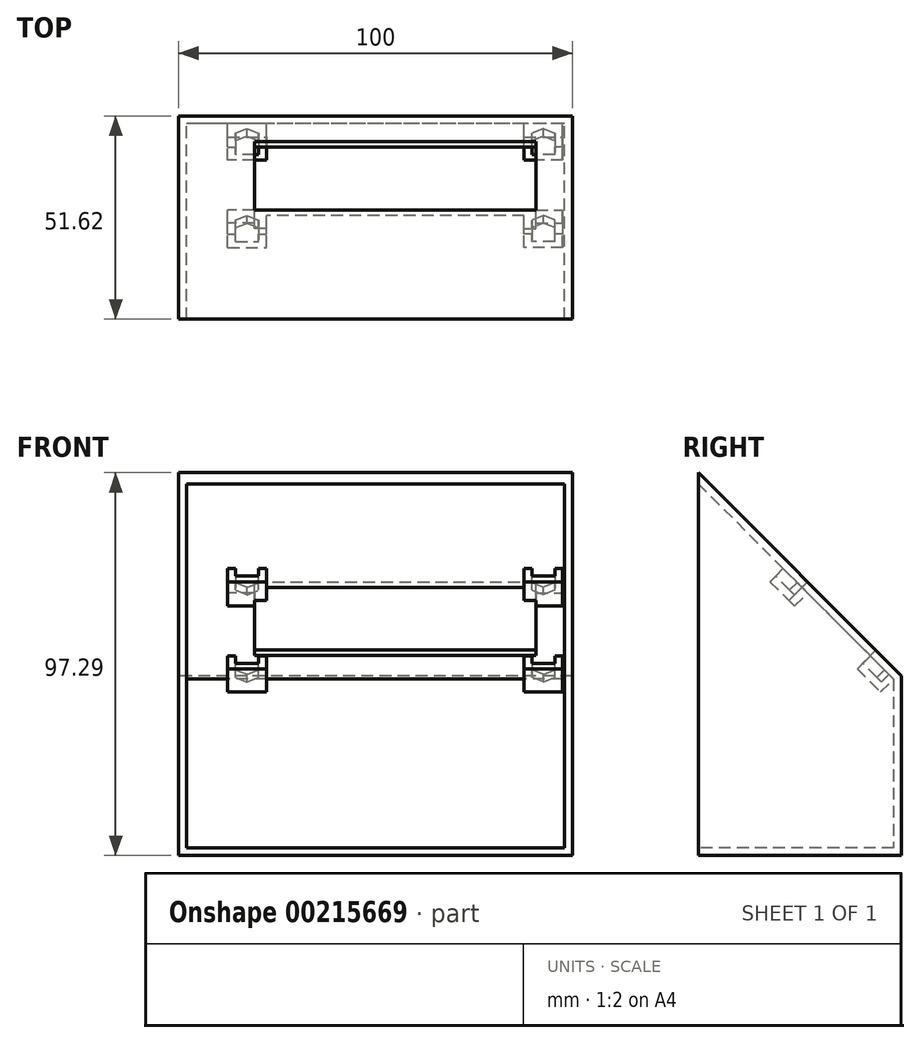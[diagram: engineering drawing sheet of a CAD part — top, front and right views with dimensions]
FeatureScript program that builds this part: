
annotation { "Feature Type Name" : "Feature", "Feature Type Description" : "" }
export const myFeature = defineFeature(function(context is Context, id is Id, definition is map)
    precondition{}
    {
        {
            var Q0;
            Q0=qCreatedBy(makeId("Top.planeOp"),FACE);
            var sketch = newSketch(context, id + "F0", { "sketchPlane" : qUnion([Q0])});
            skLineSegment(sketch, "E0.bottom", {"start": v(-35.75, 63.75) * mm, "end": v(35.75, 63.75) * mm});
            skLineSegment(sketch, "E0.top", {"start": v(-35.75, 39.25) * mm, "end": v(35.75, 39.25) * mm});
            skLineSegment(sketch, "E0.left", {"start": v(-35.75, 63.75) * mm, "end": v(-35.75, 39.25) * mm});
            skLineSegment(sketch, "E0.right", {"start": v(35.75, 63.75) * mm, "end": v(35.75, 39.25) * mm});
            skPoint(sketch, "E0.middle", {"position": v(0, 51.5) * mm});
            skLineSegment(sketch, "E1.bottom", {"start": v(-45, 73) * mm, "end": v(45, 73) * mm});
            skLineSegment(sketch, "E1.left", {"start": v(-45, 73) * mm, "end": v(-45, 30) * mm});
            skLineSegment(sketch, "E1.right", {"start": v(45, 73) * mm, "end": v(45, 30) * mm});
            skLineSegment(sketch, "E2.top", {"start": v(-45, 0) * mm, "end": v(45, 0) * mm});
            skLineSegment(sketch, "E2.left", {"start": v(-45, 30) * mm, "end": v(-45, 0) * mm});
            skLineSegment(sketch, "E2.right", {"start": v(45, 30) * mm, "end": v(45, 0) * mm});
            skSolve(sketch);
        }
        {
            var Q0;
            Q0=qCreatedBy(makeId("Right.planeOp"),FACE);
            var sketch = newSketch(context, id + "F1", { "sketchPlane" : qUnion([Q0])});
            skLineSegment(sketch, "E3", {"start": v(0, 0) * mm, "end": v(51.62, -51.62) * mm});
            skLineSegment(sketch, "E4", {"start": v(51.62, -51.62) * mm, "end": v(51.62, -97.29) * mm});
            skLineSegment(sketch, "E5", {"start": v(51.62, -97.29) * mm, "end": v(0, -97.29) * mm});
            skLineSegment(sketch, "E6", {"start": v(0, -97.29) * mm, "end": v(0, 0) * mm});
            skSolve(sketch);
        }
        {
            var Q0;
            Q0=makeQuery(id+"F1.imprint","IMPRINT",FACE,{"disambiguationData":[TD([[makeQuery(id+"F1.imprint","IMPRINT",EDGE,{"derivedFrom":sQuery(id+"F1.wireOp",EDGE,"E3")}),-1.0]])]});
            extrude(context, id + "F2", {"entities" : qUnion([Q0]), "endBound" : BoundingType.SYMMETRIC, "depth" : 90 * mm});
        }
        {
            var Q0;
            Q0=makeQuery(id+"F2.opExtrude","CAP_FACE",FACE,{"disambiguationData":[OSD([sQuery(id+"F1.wireOp",EDGE,"E3"),sQuery(id+"F1.wireOp",EDGE,"E4"),sQuery(id+"F1.wireOp",EDGE,"E5"),sQuery(id+"F1.wireOp",EDGE,"E6")])],"isStart":true});
            var sketch = newSketch(context, id + "F3", { "sketchPlane" : qUnion([Q0])});
            skLineSegment(sketch, "E7", {"start": v(-51.62, -97.29) * mm, "end": v(0, -97.29) * mm});
            skLineSegment(sketch, "E8", {"start": v(0, -97.29) * mm, "end": v(0, 0) * mm});
            skLineSegment(sketch, "E9", {"start": v(0, 0) * mm, "end": v(-51.62, -51.62) * mm});
            skLineSegment(sketch, "E10", {"start": v(-51.62, -51.62) * mm, "end": v(-51.62, -97.29) * mm});
            skSolve(sketch);
        }
        {
            var Q0;
            Q0 = qSketchRegion(id + "F3", true);
            extrude(context, id + "F4", {"entities" : qUnion([Q0]), "operationType" : NewBodyOperationType.ADD, "depth" : 10 * mm});
        }
        {
            var Q0;
            Q0=makeQuery(id+"F2.opExtrude","SWEPT_FACE",FACE,{"disambiguationData":[OSD([sQuery(id+"F1.wireOp",EDGE,"E3")])]});
            var sketch = newSketch(context, id + "F5", { "sketchPlane" : qUnion([Q0])});
            skLineSegment(sketch, "E11.bottom", {"start": v(35.75, -63.75) * mm, "end": v(-35.75, -63.75) * mm});
            skLineSegment(sketch, "E11.top", {"start": v(35.75, -39.25) * mm, "end": v(-35.75, -39.25) * mm});
            skLineSegment(sketch, "E11.left", {"start": v(35.75, -63.75) * mm, "end": v(35.75, -39.25) * mm});
            skLineSegment(sketch, "E11.right", {"start": v(-35.75, -63.75) * mm, "end": v(-35.75, -39.25) * mm});
            skPoint(sketch, "E11.middle", {"position": v(0, -51.5) * mm});
            skSolve(sketch);
        }
        {
            var Q0;
            Q0=makeQuery(id+"F2.opExtrude","SWEPT_FACE",FACE,{"disambiguationData":[OSD([sQuery(id+"F1.wireOp",EDGE,"E6")])]});
            shell(context, id + "F6", {"entities" : qUnion([Q0]), "thickness" : 2 * mm});
        }
        {
            var Q0;
            Q0=makeQuery(id+"F5.imprint","IMPRINT",FACE,{"disambiguationData":[TD([[makeQuery(id+"F5.imprint","IMPRINT",EDGE,{"derivedFrom":sQuery(id+"F5.wireOp",EDGE,"E11.bottom")}),-1.0]])]});
            extrude(context, id + "F7", {"entities" : qUnion([Q0]), "operationType" : NewBodyOperationType.REMOVE, "endBound" : BoundingType.UP_TO_NEXT, "oppositeDirection" : true, "depth" : 25 * mm});
        }
        {
            var Q0;
            Q0=makeQuery(id+"F6.opShell","OFFSET_FACE",FACE,{"disambiguationData":[OSD([sQuery(id+"F1.wireOp",EDGE,"E3")])]});
            var sketch = newSketch(context, id + "F8", { "sketchPlane" : qUnion([Q0])});
            skCircle(sketch, "E12.cCircle", {"center": v(-37.65, -35.85) * mm, "radius": 2.9 * mm, "construction": true});
            skLineSegment(sketch, "E12.0", {"start": v(-40.55, -37.52) * mm, "end": v(-40.55, -34.18) * mm, "construction": true});
            skLineSegment(sketch, "E12.1", {"start": v(-40.55, -34.18) * mm, "end": v(-37.65, -32.5) * mm, "construction": true});
            skLineSegment(sketch, "E12.2", {"start": v(-37.65, -32.5) * mm, "end": v(-34.75, -34.18) * mm, "construction": true});
            skLineSegment(sketch, "E12.3", {"start": v(-34.75, -34.18) * mm, "end": v(-34.75, -37.52) * mm, "construction": true});
            skLineSegment(sketch, "E12.4", {"start": v(-34.75, -37.52) * mm, "end": v(-37.65, -39.2) * mm, "construction": true});
            skLineSegment(sketch, "E12.5", {"start": v(-37.65, -39.2) * mm, "end": v(-40.55, -37.52) * mm, "construction": true});
            skPoint(sketch, "E12.0.midPoint", {"position": v(-40.55, -35.85) * mm});
            skCircle(sketch, "E13", {"center": v(-37.65, -35.85) * mm, "radius": 1.65 * mm, "construction": true});
            skCircle(sketch, "E14", {"center": v(37.65, -35.85) * mm, "radius": 1.65 * mm, "construction": true});
            skCircle(sketch, "E15", {"center": v(37.65, -67.15) * mm, "radius": 1.65 * mm, "construction": true});
            skCircle(sketch, "E16", {"center": v(-37.65, -67.15) * mm, "radius": 1.65 * mm, "construction": true});
            skLineSegment(sketch, "E17", {"start": v(0, -28.94) * mm, "end": v(0, -58.03) * mm});
            skLineSegment(sketch, "E18", {"start": v(0, -27.94) * mm, "end": v(0, -57.03) * mm});
            skPoint(sketch, "E19", {"position": v(-35.75, -51.5) * mm});
            skPoint(sketch, "E20", {"position": v(-37.65, -37.5) * mm});
            skLineSegment(sketch, "E21.bottom", {"start": v(-42.55, -32.5) * mm, "end": v(-40.55, -32.5) * mm});
            skLineSegment(sketch, "E21.top", {"start": v(-35.75, -39.25) * mm, "end": v(-32.75, -39.25) * mm});
            skLineSegment(sketch, "E21.left", {"start": v(-42.55, -32.5) * mm, "end": v(-42.55, -39.25) * mm});
            skLineSegment(sketch, "E21.right", {"start": v(-32.75, -32.5) * mm, "end": v(-32.75, -39.25) * mm});
            skLineSegment(sketch, "E22", {"start": v(-35.75, -39.25) * mm, "end": v(-35.75, -41.25) * mm});
            skLineSegment(sketch, "E23", {"start": v(-35.75, -41.25) * mm, "end": v(-42.55, -41.25) * mm});
            skLineSegment(sketch, "E24", {"start": v(-42.55, -41.25) * mm, "end": v(-42.55, -39.25) * mm});
            skLineSegment(sketch, "E25", {"start": v(-40.55, -32.5) * mm, "end": v(-40.55, -37.52) * mm});
            skLineSegment(sketch, "E26", {"start": v(-37.65, -39.2) * mm, "end": v(-34.75, -37.52) * mm});
            skLineSegment(sketch, "E27", {"start": v(-40.55, -37.52) * mm, "end": v(-37.65, -39.2) * mm});
            skLineSegment(sketch, "E28", {"start": v(-34.75, -37.52) * mm, "end": v(-34.75, -32.5) * mm});
            skLineSegment(sketch, "E29.trimOffspring", {"start": v(-34.75, -32.5) * mm, "end": v(-32.75, -32.5) * mm});
            skLineSegment(sketch, "E30.MirrorCS", {"start": v(40.55, -32.5) * mm, "end": v(40.55, -37.52) * mm});
            skLineSegment(sketch, "E31.MirrorCS", {"start": v(37.65, -39.2) * mm, "end": v(34.75, -37.52) * mm});
            skLineSegment(sketch, "E32.MirrorCS", {"start": v(40.55, -37.52) * mm, "end": v(37.65, -39.2) * mm});
            skLineSegment(sketch, "E33.MirrorCS", {"start": v(34.75, -37.52) * mm, "end": v(34.75, -32.5) * mm});
            skLineSegment(sketch, "E34.MirrorCS", {"start": v(40.55, -37.52) * mm, "end": v(40.55, -34.18) * mm, "construction": true});
            skLineSegment(sketch, "E35.MirrorCS", {"start": v(42.55, -41.25) * mm, "end": v(42.55, -39.25) * mm});
            skPoint(sketch, "E36.MirrorP", {"position": v(37.65, -37.5) * mm});
            skLineSegment(sketch, "E37.MirrorCS", {"start": v(32.75, -32.5) * mm, "end": v(32.75, -39.25) * mm});
            skPoint(sketch, "E38.MirrorP", {"position": v(40.55, -35.85) * mm});
            skLineSegment(sketch, "E39.MirrorCS", {"start": v(35.75, -41.25) * mm, "end": v(42.55, -41.25) * mm});
            skLineSegment(sketch, "E40.MirrorCS", {"start": v(37.65, -32.5) * mm, "end": v(34.75, -34.18) * mm, "construction": true});
            skLineSegment(sketch, "E41.MirrorCS", {"start": v(40.55, -34.18) * mm, "end": v(37.65, -32.5) * mm, "construction": true});
            skLineSegment(sketch, "E42.MirrorCS", {"start": v(42.55, -32.5) * mm, "end": v(42.55, -39.25) * mm});
            skLineSegment(sketch, "E43.MirrorCS", {"start": v(35.75, -39.25) * mm, "end": v(35.75, -41.25) * mm});
            skCircle(sketch, "E44.MirrorC", {"center": v(37.65, -35.85) * mm, "radius": 2.9 * mm, "construction": true});
            skLineSegment(sketch, "E45.MirrorCS", {"start": v(35.75, -39.25) * mm, "end": v(32.75, -39.25) * mm});
            skLineSegment(sketch, "E46.MirrorCS", {"start": v(34.75, -32.5) * mm, "end": v(32.75, -32.5) * mm});
            skLineSegment(sketch, "E47.MirrorCS", {"start": v(34.75, -37.52) * mm, "end": v(37.65, -39.2) * mm, "construction": true});
            skLineSegment(sketch, "E48.MirrorCS", {"start": v(37.65, -39.2) * mm, "end": v(40.55, -37.52) * mm, "construction": true});
            skLineSegment(sketch, "E49.MirrorCS", {"start": v(34.75, -34.18) * mm, "end": v(34.75, -37.52) * mm, "construction": true});
            skLineSegment(sketch, "E50.MirrorCS", {"start": v(42.55, -32.5) * mm, "end": v(40.55, -32.5) * mm});
            skLineSegment(sketch, "E51", {"start": v(-35.75, -51.5) * mm, "end": v(56.66, -51.5) * mm, "construction": true});
            skLineSegment(sketch, "E52.MirrorCS", {"start": v(-40.55, -68.82) * mm, "end": v(-40.55, -65.48) * mm});
            skLineSegment(sketch, "E53.MirrorCS", {"start": v(-37.65, -63.8) * mm, "end": v(-40.55, -65.48) * mm, "construction": true});
            skLineSegment(sketch, "E54.MirrorCS", {"start": v(-34.75, -65.48) * mm, "end": v(-37.65, -63.8) * mm, "construction": true});
            skLineSegment(sketch, "E55.MirrorCS", {"start": v(-34.75, -65.48) * mm, "end": v(-34.75, -68.82) * mm});
            skLineSegment(sketch, "E56.MirrorCS", {"start": v(-40.55, -68.82) * mm, "end": v(-37.65, -70.5) * mm, "construction": true});
            skLineSegment(sketch, "E57.MirrorCS", {"start": v(-37.65, -70.5) * mm, "end": v(-34.75, -68.82) * mm, "construction": true});
            skPoint(sketch, "E58.orphan", {"position": v(-40.55, -70.5) * mm});
            skPoint(sketch, "E59.orphan", {"position": v(-34.75, -70.5) * mm});
            skLineSegment(sketch, "E60", {"start": v(-40.55, -68.82) * mm, "end": v(-37.65, -70.5) * mm});
            skLineSegment(sketch, "E61", {"start": v(-37.65, -70.5) * mm, "end": v(-34.75, -68.82) * mm});
            skLineSegment(sketch, "E62.bottom", {"start": v(-42.55, -63.8) * mm, "end": v(-40.55, -63.8) * mm});
            skLineSegment(sketch, "E62.top", {"start": v(-42.55, -72.5) * mm, "end": v(-32.75, -72.5) * mm});
            skLineSegment(sketch, "E62.left", {"start": v(-42.55, -63.8) * mm, "end": v(-42.55, -72.5) * mm});
            skLineSegment(sketch, "E62.right", {"start": v(-32.75, -63.8) * mm, "end": v(-32.75, -72.5) * mm});
            skLineSegment(sketch, "E63", {"start": v(-40.55, -65.48) * mm, "end": v(-40.55, -63.8) * mm});
            skLineSegment(sketch, "E64", {"start": v(-34.75, -65.48) * mm, "end": v(-34.75, -63.75) * mm});
            skLineSegment(sketch, "E65.trimOffspring", {"start": v(-34.75, -63.8) * mm, "end": v(-32.75, -63.8) * mm});
            skLineSegment(sketch, "E66.MirrorCS", {"start": v(34.75, -65.48) * mm, "end": v(34.75, -63.75) * mm});
            skLineSegment(sketch, "E67.MirrorCS", {"start": v(34.75, -65.48) * mm, "end": v(34.75, -68.82) * mm});
            skLineSegment(sketch, "E68.MirrorCS", {"start": v(32.75, -63.8) * mm, "end": v(32.75, -72.5) * mm});
            skLineSegment(sketch, "E69.MirrorCS", {"start": v(34.75, -63.8) * mm, "end": v(32.75, -63.8) * mm});
            skLineSegment(sketch, "E70.MirrorCS", {"start": v(42.55, -72.5) * mm, "end": v(32.75, -72.5) * mm});
            skLineSegment(sketch, "E71.MirrorCS", {"start": v(42.55, -63.8) * mm, "end": v(42.55, -72.5) * mm});
            skLineSegment(sketch, "E72.MirrorCS", {"start": v(42.55, -63.8) * mm, "end": v(40.55, -63.8) * mm});
            skLineSegment(sketch, "E73.MirrorCS", {"start": v(40.55, -65.48) * mm, "end": v(40.55, -63.8) * mm});
            skLineSegment(sketch, "E74.MirrorCS", {"start": v(40.55, -68.82) * mm, "end": v(40.55, -65.48) * mm});
            skLineSegment(sketch, "E75.MirrorCS", {"start": v(40.55, -68.82) * mm, "end": v(37.65, -70.5) * mm, "construction": true});
            skLineSegment(sketch, "E76", {"start": v(37.65, -70.5) * mm, "end": v(34.75, -68.82) * mm});
            skLineSegment(sketch, "E77", {"start": v(37.65, -70.5) * mm, "end": v(40.55, -68.82) * mm});
            skSolve(sketch);
        }
        {
            var Q0;
            Q0=makeQuery(id+"F8.imprint","IMPRINT",FACE,{"disambiguationData":[TD([[makeQuery(id+"F8.imprint","IMPRINT",EDGE,{"derivedFrom":sQuery(id+"F8.wireOp",EDGE,"E52.MirrorCS")}),1.0]])]});
            var Q1;
            Q1=makeQuery(id+"F8.imprint","IMPRINT",FACE,{"disambiguationData":[TD([[makeQuery(id+"F8.imprint","IMPRINT",EDGE,{"derivedFrom":sQuery(id+"F8.wireOp",EDGE,"E21.bottom")}),-1.0]])]});
            var Q2;
            Q2=makeQuery(id+"F8.imprint","IMPRINT",FACE,{"disambiguationData":[TD([[makeQuery(id+"F8.imprint","IMPRINT",EDGE,{"derivedFrom":sQuery(id+"F8.wireOp",EDGE,"E30.MirrorCS")}),1.0]])]});
            var Q3;
            {var subQ4=sQuery(id+"F8.wireOp",EDGE,"E67.MirrorCS");Q3=makeQuery(id+"F8.imprint","IMPRINT",FACE,{"disambiguationData":[TD([[makeQuery(id+"F8.imprint","IMPRINT",EDGE,{"derivedFrom":subQ4}),-1.0]])]});}
            extrude(context, id + "F9", {"entities" : qUnion([Q0, Q1, Q2, Q3]), "operationType" : NewBodyOperationType.ADD, "depth" : 2.7 * mm});
        }
        {
            var Q0;
            Q0=makeQuery(id+"F9.opExtrude","CAP_FACE",FACE,{"disambiguationData":[OSD([sQuery(id+"F8.wireOp",EDGE,"E21.bottom"),sQuery(id+"F8.wireOp",EDGE,"E21.top"),sQuery(id+"F8.wireOp",EDGE,"E21.left"),sQuery(id+"F8.wireOp",EDGE,"E21.right"),sQuery(id+"F8.wireOp",EDGE,"E22"),sQuery(id+"F8.wireOp",EDGE,"E23"),sQuery(id+"F8.wireOp",EDGE,"E24"),sQuery(id+"F8.wireOp",EDGE,"E25"),sQuery(id+"F8.wireOp",EDGE,"E26"),sQuery(id+"F8.wireOp",EDGE,"E27"),sQuery(id+"F8.wireOp",EDGE,"E28"),sQuery(id+"F8.wireOp",EDGE,"E29.trimOffspring")])],"isStart":false});
            var sketch = newSketch(context, id + "F10", { "sketchPlane" : qUnion([Q0])});
            skLineSegment(sketch, "E78.bottom", {"start": v(-42.55, -41.25) * mm, "end": v(-35.75, -41.25) * mm});
            skLineSegment(sketch, "E78.top", {"start": v(-42.55, -32.5) * mm, "end": v(-32.75, -32.5) * mm});
            skLineSegment(sketch, "E78.left", {"start": v(-42.55, -41.25) * mm, "end": v(-42.55, -32.5) * mm});
            skLineSegment(sketch, "E78.right", {"start": v(-32.75, -39.25) * mm, "end": v(-32.75, -32.5) * mm});
            skLineSegment(sketch, "E79.0.0", {"start": v(35.75, -39.25) * mm, "end": v(35.75, -41.25) * mm});
            skLineSegment(sketch, "E79.0.1", {"start": v(35.75, -41.25) * mm, "end": v(42.55, -41.25) * mm});
            skLineSegment(sketch, "E79.0.2", {"start": v(42.55, -41.25) * mm, "end": v(42.55, -32.5) * mm});
            skLineSegment(sketch, "E79.0.3", {"start": v(42.55, -32.5) * mm, "end": v(40.55, -32.5) * mm});
            skLineSegment(sketch, "E79.0.4", {"start": v(40.55, -32.5) * mm, "end": v(40.55, -37.52) * mm});
            skLineSegment(sketch, "E79.0.5", {"start": v(40.55, -37.52) * mm, "end": v(37.65, -39.2) * mm});
            skLineSegment(sketch, "E79.0.6", {"start": v(37.65, -39.2) * mm, "end": v(34.75, -37.52) * mm});
            skLineSegment(sketch, "E79.0.7", {"start": v(34.75, -37.52) * mm, "end": v(34.75, -32.5) * mm});
            skLineSegment(sketch, "E79.0.8", {"start": v(34.75, -32.5) * mm, "end": v(32.75, -32.5) * mm});
            skLineSegment(sketch, "E79.0.9", {"start": v(32.75, -32.5) * mm, "end": v(32.75, -39.25) * mm});
            skLineSegment(sketch, "E79.0.10", {"start": v(32.75, -39.25) * mm, "end": v(35.75, -39.25) * mm});
            skLineSegment(sketch, "E80.0.0", {"start": v(34.75, -68.82) * mm, "end": v(34.75, -63.8) * mm});
            skLineSegment(sketch, "E80.0.1", {"start": v(34.75, -63.8) * mm, "end": v(32.75, -63.8) * mm});
            skLineSegment(sketch, "E80.0.2", {"start": v(32.75, -63.8) * mm, "end": v(32.75, -72.17) * mm});
            skLineSegment(sketch, "E80.0.3", {"start": v(32.75, -72.17) * mm, "end": v(42.55, -72.17) * mm});
            skLineSegment(sketch, "E80.0.4", {"start": v(42.55, -72.17) * mm, "end": v(42.55, -63.8) * mm});
            skLineSegment(sketch, "E80.0.5", {"start": v(42.55, -63.8) * mm, "end": v(40.55, -63.8) * mm});
            skLineSegment(sketch, "E80.0.6", {"start": v(40.55, -63.8) * mm, "end": v(40.55, -68.82) * mm});
            skLineSegment(sketch, "E80.0.7", {"start": v(40.55, -68.82) * mm, "end": v(37.65, -70.5) * mm});
            skLineSegment(sketch, "E80.0.8", {"start": v(37.65, -70.5) * mm, "end": v(34.75, -68.82) * mm});
            skPoint(sketch, "E81.0", {"position": v(-40.55, -66.31) * mm});
            skLineSegment(sketch, "E82.0.0", {"start": v(-32.75, -72.17) * mm, "end": v(-32.75, -63.8) * mm});
            skLineSegment(sketch, "E82.0.1", {"start": v(-32.75, -63.8) * mm, "end": v(-34.75, -63.8) * mm});
            skLineSegment(sketch, "E82.0.2", {"start": v(-34.75, -63.8) * mm, "end": v(-34.75, -68.82) * mm});
            skLineSegment(sketch, "E82.0.3", {"start": v(-34.75, -68.82) * mm, "end": v(-37.65, -70.5) * mm});
            skLineSegment(sketch, "E82.0.4", {"start": v(-37.65, -70.5) * mm, "end": v(-40.55, -68.82) * mm});
            skLineSegment(sketch, "E82.0.5", {"start": v(-40.55, -68.82) * mm, "end": v(-40.55, -63.8) * mm});
            skLineSegment(sketch, "E82.0.6", {"start": v(-40.55, -63.8) * mm, "end": v(-42.55, -63.8) * mm});
            skLineSegment(sketch, "E82.0.7", {"start": v(-42.55, -63.8) * mm, "end": v(-42.55, -72.17) * mm});
            skLineSegment(sketch, "E82.0.8", {"start": v(-42.55, -72.17) * mm, "end": v(-32.75, -72.17) * mm});
            skLineSegment(sketch, "E83.bottom", {"start": v(-42.55, -63.8) * mm, "end": v(-32.75, -63.8) * mm});
            skLineSegment(sketch, "E83.right", {"start": v(-32.75, -63.8) * mm, "end": v(-32.75, -72.17) * mm});
            skLineSegment(sketch, "E84.bottom", {"start": v(32.75, -32.5) * mm, "end": v(42.55, -32.5) * mm});
            skLineSegment(sketch, "E84.right", {"start": v(42.55, -32.5) * mm, "end": v(42.55, -41.25) * mm});
            skLineSegment(sketch, "E85.bottom", {"start": v(32.75, -63.8) * mm, "end": v(42.55, -63.8) * mm});
            skLineSegment(sketch, "E85.right", {"start": v(42.55, -63.8) * mm, "end": v(42.55, -72.17) * mm});
            skLineSegment(sketch, "E86", {"start": v(35.75, -41.25) * mm, "end": v(35.75, -39.25) * mm});
            skLineSegment(sketch, "E87", {"start": v(-32.75, -39.25) * mm, "end": v(-35.75, -39.25) * mm});
            skLineSegment(sketch, "E88", {"start": v(-35.75, -39.25) * mm, "end": v(-35.75, -41.25) * mm});
            skSolve(sketch);
        }
        {
            var Q0;
            Q0 = qSketchRegion(id + "F10", true);
            extrude(context, id + "F11", {"entities" : qUnion([Q0]), "operationType" : NewBodyOperationType.ADD, "depth" : 2 * mm});
        }
    });
